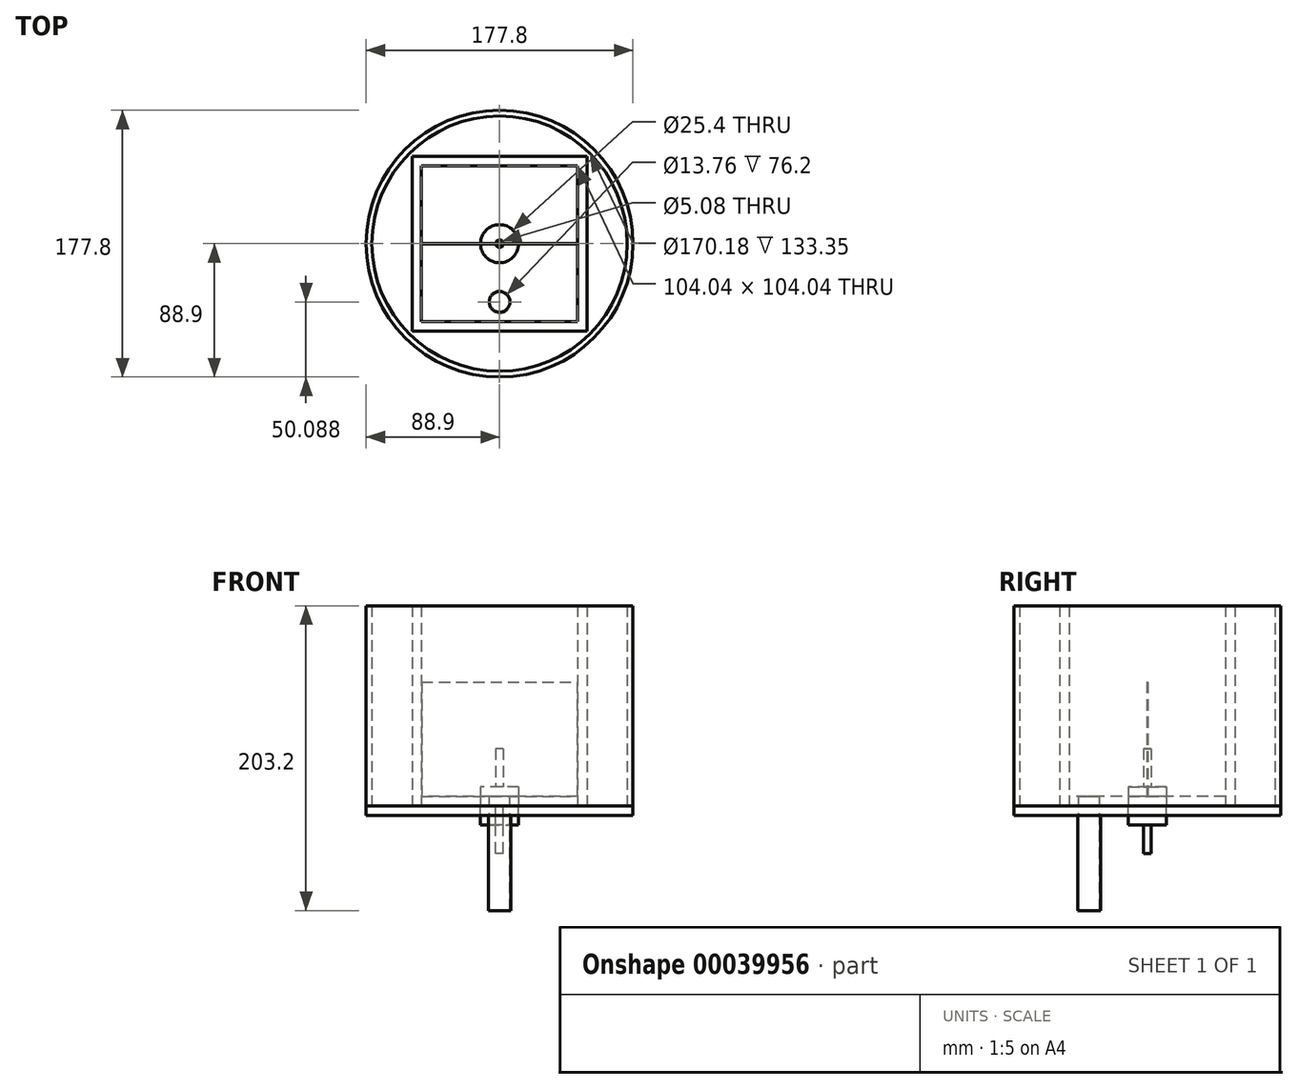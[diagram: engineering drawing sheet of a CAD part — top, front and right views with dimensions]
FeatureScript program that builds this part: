
annotation { "Feature Type Name" : "Feature", "Feature Type Description" : "" }
export const myFeature = defineFeature(function(context is Context, id is Id, definition is map)
    precondition{}
    {
        {
            var Q0;
            Q0=qCreatedBy(makeId("Top.planeOp"),FACE);
            var sketch = newSketch(context, id + "F0", { "sketchPlane" : qUnion([Q0])});
            skCircle(sketch, "E0.0", {"center": v(0, 0) * mm, "radius": 88.9 * mm});
            skLineSegment(sketch, "E1", {"start": v(-58.37, 58.37) * mm, "end": v(-58.37, -58.37) * mm});
            skLineSegment(sketch, "E2", {"start": v(-58.37, -58.37) * mm, "end": v(58.37, -58.37) * mm});
            skLineSegment(sketch, "E3", {"start": v(58.37, -58.37) * mm, "end": v(58.37, 58.37) * mm});
            skLineSegment(sketch, "E4", {"start": v(58.37, 58.37) * mm, "end": v(-58.37, 58.37) * mm});
            skLineSegment(sketch, "E5.0", {"start": v(-52.02, 52.02) * mm, "end": v(-52.02, -52.02) * mm});
            skLineSegment(sketch, "E6.0", {"start": v(52.02, 52.02) * mm, "end": v(-52.02, 52.02) * mm});
            skLineSegment(sketch, "E7.0", {"start": v(52.02, -52.02) * mm, "end": v(52.02, 52.02) * mm});
            skLineSegment(sketch, "E8.0", {"start": v(-52.02, -52.02) * mm, "end": v(52.02, -52.02) * mm});
            skCircle(sketch, "E9.0", {"center": v(0, 0) * mm, "radius": 85.1 * mm});
            skCircle(sketch, "E10", {"center": v(0, 0) * mm, "radius": 12.7 * mm});
            skCircle(sketch, "E11", {"center": v(0, 0) * mm, "radius": 2.54 * mm});
            skSolve(sketch);
        }
        {
            var Q0;
            Q0=makeQuery(id+"F0.imprint","IMPRINT",FACE,{"disambiguationData":[TD([[makeQuery(id+"F0.imprint","IMPRINT",EDGE,{"derivedFrom":sQuery(id+"F0.wireOp",EDGE,"E0.0")}),1.0]])]});
            extrude(context, id + "F1", {"entities" : qUnion([Q0]), "depth" : 133.35 * mm});
        }
        {
            var Q0;
            Q0=makeQuery(id+"F0.imprint","IMPRINT",FACE,{"disambiguationData":[TD([[makeQuery(id+"F0.imprint","IMPRINT",EDGE,{"derivedFrom":sQuery(id+"F0.wireOp",EDGE,"E1")}),1.0]])]});
            extrude(context, id + "F2", {"entities" : qUnion([Q0]), "depth" : 133.35 * mm});
        }
        {
            var Q0;
            Q0=makeQuery(id+"F0.imprint","IMPRINT",FACE,{"disambiguationData":[TD([[makeQuery(id+"F0.imprint","IMPRINT",EDGE,{"derivedFrom":sQuery(id+"F0.wireOp",EDGE,"E10")}),1.0]])]});
            extrude(context, id + "F3", {"entities" : qUnion([Q0]), "depth" : 12.7 * mm});
        }
        {
            var Q0;
            Q0=makeQuery(id+"F0.imprint","IMPRINT",FACE,{"disambiguationData":[TD([[makeQuery(id+"F0.imprint","IMPRINT",EDGE,{"derivedFrom":sQuery(id+"F0.wireOp",EDGE,"E5.0")}),1.0]])]});
            extrude(context, id + "F4", {"entities" : qUnion([Q0]), "depth" : 6.35 * mm});
        }
        {
            var Q0;
            Q0=makeQuery(id+"F0.imprint","IMPRINT",FACE,{"disambiguationData":[TD([[makeQuery(id+"F0.imprint","IMPRINT",EDGE,{"derivedFrom":sQuery(id+"F0.wireOp",EDGE,"E11")}),1.0]])]});
            extrude(context, id + "F5", {"entities" : qUnion([Q0]), "operationType" : NewBodyOperationType.ADD, "depth" : 38.1 * mm});
        }
        {
            var Q0;
            Q0=makeQuery(id+"F0.imprint","IMPRINT",FACE,{"disambiguationData":[TD([[makeQuery(id+"F0.imprint","IMPRINT",EDGE,{"derivedFrom":sQuery(id+"F0.wireOp",EDGE,"E0.0")}),1.0]])]});
            var Q1;
            Q1=makeQuery(id+"F0.imprint","IMPRINT",FACE,{"disambiguationData":[TD([[makeQuery(id+"F0.imprint","IMPRINT",EDGE,{"derivedFrom":sQuery(id+"F0.wireOp",EDGE,"E1")}),-1.0]])]});
            var Q2;
            Q2=makeQuery(id+"F0.imprint","IMPRINT",FACE,{"disambiguationData":[TD([[makeQuery(id+"F0.imprint","IMPRINT",EDGE,{"derivedFrom":sQuery(id+"F0.wireOp",EDGE,"E1")}),1.0]])]});
            var Q3;
            Q3=makeQuery(id+"F0.imprint","IMPRINT",FACE,{"disambiguationData":[TD([[makeQuery(id+"F0.imprint","IMPRINT",EDGE,{"derivedFrom":sQuery(id+"F0.wireOp",EDGE,"E5.0")}),1.0]])]});
            extrude(context, id + "F6", {"entities" : qUnion([Q0, Q1, Q2, Q3]), "oppositeDirection" : true, "depth" : 6.35 * mm});
        }
        {
            var Q0;
            Q0=makeQuery(id+"F0.imprint","IMPRINT",FACE,{"disambiguationData":[TD([[makeQuery(id+"F0.imprint","IMPRINT",EDGE,{"derivedFrom":sQuery(id+"F0.wireOp",EDGE,"E11")}),1.0]])]});
            extrude(context, id + "F7", {"entities" : qUnion([Q0]), "operationType" : NewBodyOperationType.ADD, "oppositeDirection" : true, "depth" : 31.75 * mm});
        }
        {
            var Q0;
            Q0=makeQuery(id+"F0.imprint","IMPRINT",FACE,{"disambiguationData":[TD([[makeQuery(id+"F0.imprint","IMPRINT",EDGE,{"derivedFrom":sQuery(id+"F0.wireOp",EDGE,"E10")}),1.0]])]});
            extrude(context, id + "F8", {"entities" : qUnion([Q0]), "oppositeDirection" : true, "depth" : 12.7 * mm});
        }
        {
            var Q0;
            Q0=makeQuery(id+"F4.opExtrude","CAP_FACE",FACE,{"disambiguationData":[OSD([sQuery(id+"F0.wireOp",EDGE,"E5.0"),sQuery(id+"F0.wireOp",EDGE,"E6.0"),sQuery(id+"F0.wireOp",EDGE,"E7.0"),sQuery(id+"F0.wireOp",EDGE,"E8.0"),sQuery(id+"F0.wireOp",EDGE,"E10")])],"isStart":false});
            var sketch = newSketch(context, id + "F9", { "sketchPlane" : qUnion([Q0])});
            skCircle(sketch, "E12", {"center": v(0, -38.81) * mm, "radius": 6.88 * mm});
            skCircle(sketch, "E13.0", {"center": v(0, -38.81) * mm, "radius": 7.58 * mm});
            skSolve(sketch);
        }
        {
            var Q0;
            Q0=makeQuery(id+"F9.imprint","IMPRINT",FACE,{"disambiguationData":[TD([[makeQuery(id+"F9.imprint","IMPRINT",EDGE,{"derivedFrom":sQuery(id+"F9.wireOp",EDGE,"E12")}),-1.0]])]});
            extrude(context, id + "F10", {"entities" : qUnion([Q0]), "operationType" : NewBodyOperationType.ADD, "oppositeDirection" : true, "depth" : 76.2 * mm});
        }
        {
            var Q0;
            Q0=makeQuery(id+"F9.imprint","IMPRINT",FACE,{"disambiguationData":[TD([[makeQuery(id+"F9.imprint","IMPRINT",EDGE,{"derivedFrom":sQuery(id+"F9.wireOp",EDGE,"E12")}),1.0]])]});
            extrude(context, id + "F11", {"entities" : qUnion([Q0]), "operationType" : NewBodyOperationType.REMOVE, "endBound" : BoundingType.THROUGH_ALL, "oppositeDirection" : true, "depth" : 76.2 * mm});
        }
        {
            var Q0;
            Q0=makeQuery(id+"F9.imprint","IMPRINT",FACE,{"disambiguationData":[TD([[makeQuery(id+"F9.imprint","IMPRINT",EDGE,{"derivedFrom":sQuery(id+"F9.wireOp",EDGE,"E12")}),1.0]])]});
            extrude(context, id + "F12", {"entities" : qUnion([Q0]), "operationType" : NewBodyOperationType.REMOVE, "oppositeDirection" : true, "depth" : 12.7 * mm});
        }
        {
            var Q0;
            Q0=makeQuery(id+"F9.imprint","IMPRINT",FACE,{"disambiguationData":[TD([[makeQuery(id+"F9.imprint","IMPRINT",EDGE,{"derivedFrom":sQuery(id+"F9.wireOp",EDGE,"E12")}),1.0]])]});
            var sketch = newSketch(context, id + "F13", { "sketchPlane" : qUnion([Q0])});
            skLineSegment(sketch, "E14.bottom", {"start": v(-51.96, -0.25) * mm, "end": v(51.62, -0.25) * mm});
            skLineSegment(sketch, "E14.top", {"start": v(-51.96, 0.26) * mm, "end": v(51.62, 0.26) * mm});
            skLineSegment(sketch, "E14.left", {"start": v(-51.96, -0.25) * mm, "end": v(-51.96, 0.26) * mm});
            skLineSegment(sketch, "E14.right", {"start": v(51.62, -0.25) * mm, "end": v(51.62, 0.26) * mm});
            skSolve(sketch);
        }
        {
            var Q0;
            Q0 = qSketchRegion(id + "F13", true);
            extrude(context, id + "F14", {"entities" : qUnion([Q0]), "depth" : 76.2 * mm});
        }
    });
